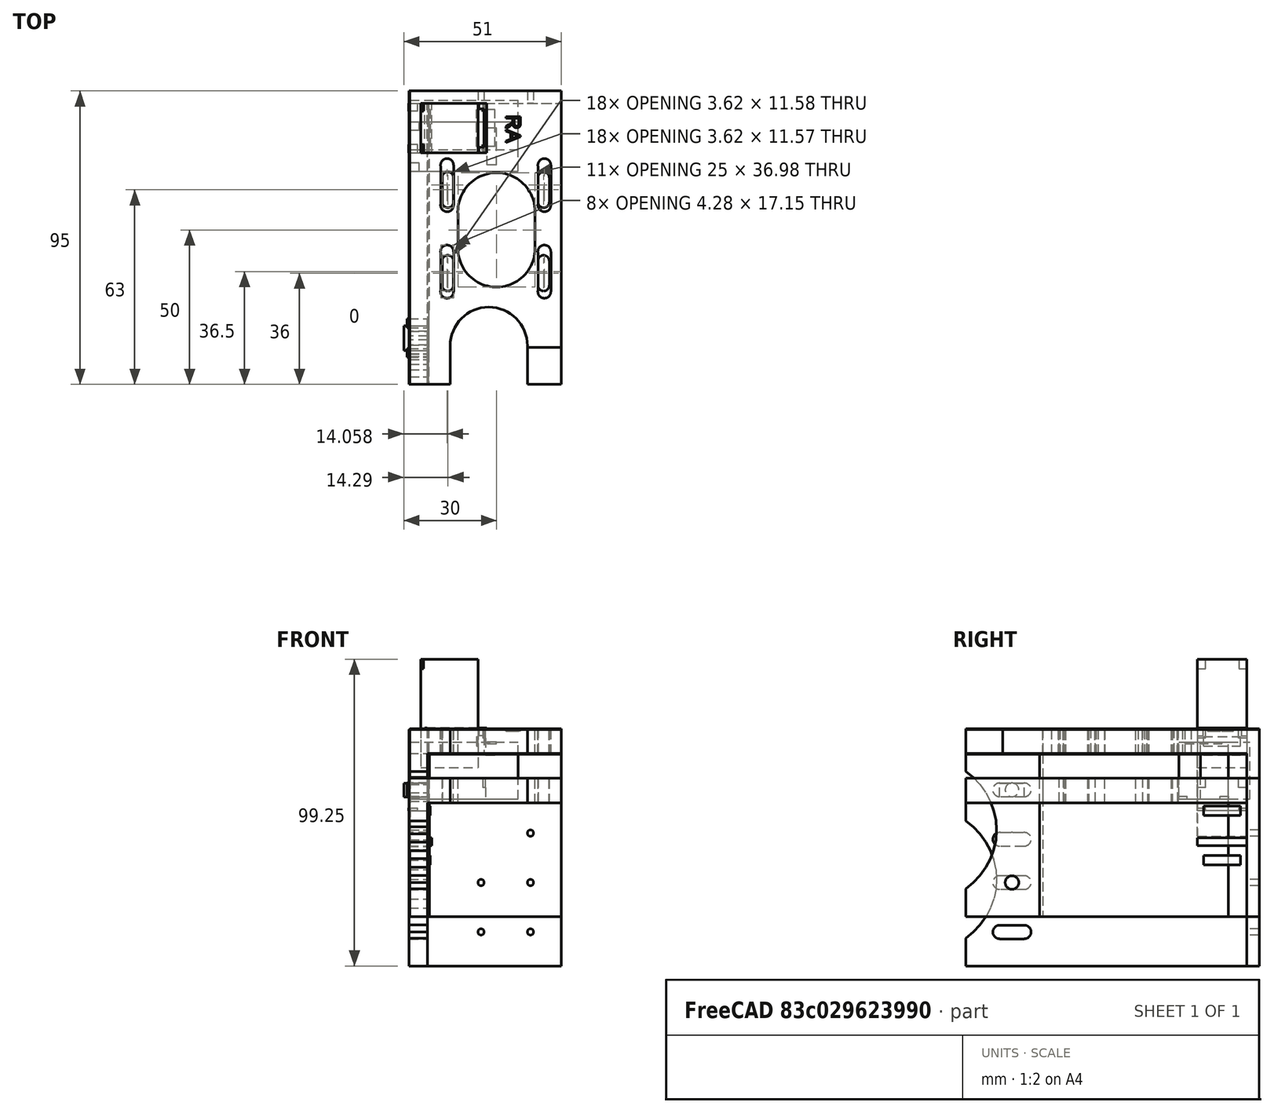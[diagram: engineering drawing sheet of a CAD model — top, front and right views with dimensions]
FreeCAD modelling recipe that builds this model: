
FCSTD DOCUMENT  (FreeCAD 0.17R11223 (Git))
Label: EQ-motorvRAv2
License: All rights reserved
LicenseURL: http://en.wikipedia.org/wiki/All_rights_reserved
objects: Part::Feature×21, Part::Box×16, Part::Cut×14, Part::Cylinder×12, Part::MultiFuse×11, Part::Extrusion×3, Part::Part2DObjectPython×1
note: 78 computed .brp shape members not serialized (recipe doc carries the construction recipe); baked Part::Feature solids carry a one-line shape summary decoded from their .brp

FEATURE [Part::Feature] Cut026_solid  label="zadni stena (Solid)"
  shape: bbox 49 x 4 x 60.5 mm, 8 faces (baked)
FEATURE [Part::Feature] Fusion008_solid  label="Boky"
  shape: bbox 49 x 85 x 60.5 mm, 76 faces (baked)
FEATURE [Part::Box] Box005009  label="Krychle009"
  AttacherType = Attacher::AttachEngine3D
  Height = 18.5
  Length = 35
  Placement = pos=(-5,75,-44) rot=(0,0,1;0rad)
  Width = 16
FEATURE [Part::Box] Box005011  label="Krychle010"
  AttacherType = Attacher::AttachEngine3D
  Height = 2.7
  Length = 3
  Placement = pos=(-5,75,-45.8) rot=(0,0,1;0rad)
  Width = 2.7
FEATURE [Part::Box] Box005012  label="Krychle011"
  AttacherType = Attacher::AttachEngine3D
  Height = 2.7
  Length = 3
  Placement = pos=(-5,88.4,-45.8) rot=(0,0,1;0rad)
  Width = 2.7
FEATURE [Part::Box] Box005014  label="Krychle013"
  AttacherType = Attacher::AttachEngine3D
  Height = 2
  Length = 3
  Placement = pos=(20,77,-26) rot=(0,0,1;0rad)
  Width = 12
FEATURE [Part::Box] Box005015  label="Pro RJ"
  AttacherType = Attacher::AttachEngine3D
  Height = 18.5
  Length = 35
  Placement = pos=(-5,82,-44) rot=(0,0,1;0rad)
  Width = 16
FEATURE [Part::Box] Box005016  label="Krychle014"
  AttacherType = Attacher::AttachEngine3D
  Height = 8
  Length = 49
  Placement = pos=(-5,91,-29.5) rot=(0,0,1;0rad)
  Width = 6
FEATURE [Part::Box] Box005017  label="Krychle015"
  AttacherType = Attacher::AttachEngine3D
  Height = 60
  Length = 6
  Placement = pos=(-5,91,-82) rot=(0,0,1;0rad)
  Width = 6
FEATURE [Part::MultiFuse] Fusion
  Shapes = -> [Box005017,Box005016,Cut026_solid,Fusion008_solid]
FEATURE [Part::Feature] Fusion_solid  label="Fusion (Solid)"
  shape: bbox 49 x 95 x 60.5 mm, 91 faces (baked)
FEATURE [Part::Feature] Fusion_solid001  label="Fusion (Solid)001"
  shape: bbox 49 x 95 x 60.5 mm, 72 faces (baked)
FEATURE [Part::Feature] Fusion_solid_cs  label="REZ A"
  shape: bbox 49 x 95 x 4e-07 mm, 0 faces, 0 solids (baked)
FEATURE [Part::Feature] Fusion_solid001_cs  label="REZ B"
  shape: bbox 5e-07 x 95 x 60.5 mm, 0 faces, 0 solids (baked)
FEATURE [Part::Feature] Cut026_solid001  label="zadni stena (Solid)001"
  shape: bbox 49 x 4 x 60.5 mm, 8 faces (baked)
FEATURE [Part::Extrusion] Extrude  label="Vrsek"
  Base = -> Fusion_solid_cs
  Dir = (0,0,1)
  DirMode = 2
  FaceMakerClass = Part::FaceMakerBullseye
  LengthFwd = 8
  LengthRev = 0
  Placement = pos=(0,0,-2.5) rot=(0,0,1;0rad)
  Solid = true
  Symmetric = false
FEATURE [Part::Extrusion] Extrude001  label="Bok"
  Base = -> Fusion_solid001_cs
  Dir = (1,0,0)
  DirMode = 2
  FaceMakerClass = Part::FaceMakerBullseye
  LengthFwd = 6
  LengthRev = 0
  Placement = pos=(-1.8,0,0) rot=(0,0,1;0rad)
  Solid = true
  Symmetric = false
FEATURE [Part::MultiFuse] Fusion001
  Shapes = -> [Cut026_solid001,Extrude,Extrude001]
FEATURE [Part::Feature] Fusion001001  label="Fusion002"
  shape: bbox 49.3 x 95 x 60.75 mm, 66 faces (baked)
FEATURE [Part::Feature] Fusion001001_solid  label="Drzak Bez RJ"
  shape: bbox 49.3 x 95 x 60.75 mm, 66 faces (baked)
FEATURE [Part::Box] Box005018  label="Krychle016"
  AttacherType = Attacher::AttachEngine3D
  Height = 16
  Length = 31.5
  Placement = pos=(1,81,-22) rot=(0,1,0;1.5708rad)
  Width = 15.5
FEATURE [Part::Cut] Cut
  Base = -> Box005009
  Tool = -> Box005011
FEATURE [Part::Cut] Cut001
  Base = -> Cut
  Tool = -> Box005012
FEATURE [Part::Cut] Cut002  label="Pro RJ001"
  Base = -> Cut001
  Tool = -> Box005014
FEATURE [Part::Feature] Cut002_solid  label="Pro RJ001 (Solid)"
  Placement = pos=(42.5,6,-3.75) rot=(0,1,0;1.5708rad)
  shape: bbox 18.5 x 16 x 35 mm, 17 faces (baked)
FEATURE [Part::Feature] Cut003001_solid  label="EQ motorDe V3"
  shape: bbox 49.5 x 95 x 60.75 mm, 85 faces (baked)
FEATURE [Part::Feature] Cut002_solid001  label="Pro RJ001 (Solid)001"
  Placement = pos=(18,178,-22.5) rot=(0,0,1;3.14159rad)
  shape: bbox 18.5 x 16 x 35 mm, 17 faces (baked)
FEATURE [Part::MultiFuse] Fusion001002
  Shapes = -> [Box005018,Fusion001001_solid]
FEATURE [Part::Cut] Cut003
  Base = -> Fusion001002
  Tool = -> Cut002_solid001
FEATURE [Part::Feature] Cut003001  label="RA V2"
  shape: bbox 49.3 x 95 x 60.75 mm, 81 faces, 2 solids (baked)
FEATURE [Part::Cylinder] Cylinder  label="Válec"
  Angle = 360
  AttacherType = Attacher::AttachEngine3D
  Height = 7
  Placement = pos=(-6,25,-41) rot=(0,1,0;1.5708rad)
  Radius = 2.2
FEATURE [Part::Cylinder] Cylinder001  label="Válec001"
  Angle = 360
  AttacherType = Attacher::AttachEngine3D
  Height = 7
  Placement = pos=(-6,17,-41) rot=(0,1,0;1.5708rad)
  Radius = 2.2
FEATURE [Part::Box] Box  label="Krychle"
  AttacherType = Attacher::AttachEngine3D
  Height = 4.4
  Length = 8
  Placement = pos=(-7,17,-43.3) rot=(0,0,1;0rad)
  Width = 8
FEATURE [Part::MultiFuse] Fusion001003
  Shapes = -> [Cylinder001,Cylinder,Box]
FEATURE [Part::Feature] Fusion001003001  label="DIRA 010"
  shape: bbox 8 x 12.4 x 4.5 mm, 10 faces (baked)
FEATURE [Part::Feature] Fusion001003002  label="DIRA 011"
  Placement = pos=(0,0,-30) rot=(0,0,1;0rad)
  shape: bbox 8 x 12.4 x 4.5 mm, 10 faces (baked)
FEATURE [Part::Cut] Cut003002
  Base = -> Cut003001
  Tool = -> Fusion001003001
FEATURE [Part::Cut] Cut003003
  Base = -> Cut003002
  Placement = pos=(0,0,-16) rot=(0,0,1;0rad)
  Tool = -> Fusion001003002
FEATURE [Part::Feature] Cut003003001  label="RA V4"
  shape: bbox 49.3 x 95 x 60.75 mm, 95 faces, 2 solids (baked)
FEATURE [Part::Box] Box005019  label="Krychle017"
  AttacherType = Attacher::AttachEngine3D
  Height = 10
  Length = 15
  Placement = pos=(31,5,-30) rot=(0,0,1;0rad)
  Width = 13
FEATURE [Part::Cut] Cut003003002
  Base = -> Cut003003001
  Tool = -> Box005019
FEATURE [Part::Feature] Cut003003002001  label="Cut003003003"
  shape: bbox 49.3 x 95 x 60.75 mm, 95 faces, 2 solids (baked)
FEATURE [Part::Cylinder] Cylinder002  label="Válec002"
  Angle = 360
  AttacherType = Attacher::AttachEngine3D
  Height = 4
  Placement = pos=(18,101,-71) rot=(1,0,0;1.5708rad)
  Radius = 1
FEATURE [Part::Cylinder] Cylinder003  label="Válec003"
  Angle = 360
  AttacherType = Attacher::AttachEngine3D
  Height = 4
  Placement = pos=(34,101,-55) rot=(1,0,0;1.5708rad)
  Radius = 1
FEATURE [Part::MultiFuse] Fusion001003003
  Shapes = -> [Cut003003002001,Cylinder002]
FEATURE [Part::Cut] Cut003003002002
  Base = -> Fusion001003003
  Tool = -> Cylinder003
FEATURE [Part::Feature] Cut003003002002001  label="EQ RA V3"
  shape: bbox 49.3 x 95 x 60.75 mm, 95 faces, 2 solids (baked)
FEATURE [Part::Cylinder] Cylinder004  label="Válec004"
  Angle = 360
  AttacherType = Attacher::AttachEngine3D
  Height = 10
  Radius = 2.1
FEATURE [Part::Cylinder] Cylinder005  label="Válec005"
  Angle = 360
  AttacherType = Attacher::AttachEngine3D
  Height = 10
  Placement = pos=(0,13,0) rot=(0,0,1;0rad)
  Radius = 2.1
FEATURE [Part::Box] Box005020  label="Krychle018"
  AttacherType = Attacher::AttachEngine3D
  Height = 10
  Length = 4.2
  Placement = pos=(-2,0,0) rot=(0,0,1;0rad)
  Width = 13
FEATURE [Part::MultiFuse] Fusion001003004  label="Dira M"
  Placement = pos=(7,36,-30) rot=(0,0,1;0rad)
  Shapes = -> [Cylinder004,Cylinder005,Box005020]
FEATURE [Part::Cylinder] Cylinder006  label="Válec006"
  Angle = 360
  AttacherType = Attacher::AttachEngine3D
  Height = 10
  Radius = 2.1
FEATURE [Part::Cylinder] Cylinder007  label="Válec007"
  Angle = 360
  AttacherType = Attacher::AttachEngine3D
  Height = 10
  Placement = pos=(0,13,0) rot=(0,0,1;0rad)
  Radius = 2.1
FEATURE [Part::Box] Box005021  label="Krychle019"
  AttacherType = Attacher::AttachEngine3D
  Height = 10
  Length = 4.2
  Placement = pos=(-2,0,0) rot=(0,0,1;0rad)
  Width = 13
FEATURE [Part::MultiFuse] Fusion001003005  label="Dira M001"
  Placement = pos=(38.5,36,-30) rot=(0,0,1;0rad)
  Shapes = -> [Cylinder006,Cylinder007,Box005021]
FEATURE [Part::Cylinder] Cylinder008  label="Válec008"
  Angle = 360
  AttacherType = Attacher::AttachEngine3D
  Height = 10
  Radius = 2.1
FEATURE [Part::Cylinder] Cylinder009  label="Válec009"
  Angle = 360
  AttacherType = Attacher::AttachEngine3D
  Height = 10
  Placement = pos=(0,13,0) rot=(0,0,1;0rad)
  Radius = 2.1
FEATURE [Part::Box] Box005022  label="Krychle020"
  AttacherType = Attacher::AttachEngine3D
  Height = 10
  Length = 4.2
  Placement = pos=(-2,0,0) rot=(0,0,1;0rad)
  Width = 13
FEATURE [Part::MultiFuse] Fusion001003006  label="Dira M002"
  Placement = pos=(7,64,-30) rot=(0,0,1;0rad)
  Shapes = -> [Cylinder008,Cylinder009,Box005022]
FEATURE [Part::Cylinder] Cylinder010  label="Válec010"
  Angle = 360
  AttacherType = Attacher::AttachEngine3D
  Height = 10
  Radius = 2.1
FEATURE [Part::Cylinder] Cylinder011  label="Válec011"
  Angle = 360
  AttacherType = Attacher::AttachEngine3D
  Height = 10
  Placement = pos=(0,13,0) rot=(0,0,1;0rad)
  Radius = 2.1
FEATURE [Part::Box] Box005023  label="Krychle021"
  AttacherType = Attacher::AttachEngine3D
  Height = 10
  Length = 4.2
  Placement = pos=(-2,0,0) rot=(0,0,1;0rad)
  Width = 13
FEATURE [Part::MultiFuse] Fusion001003007  label="Dira M003"
  Placement = pos=(38.5,64,-30) rot=(0,0,1;0rad)
  Shapes = -> [Cylinder010,Cylinder011,Box005023]
FEATURE [Part::Box] Box009  label="Doraz003"
  AttacherType = Attacher::AttachEngine3D
  Height = 2.5
  Length = 2
  Placement = pos=(0,81,-59) rot=(0,0,1;0rad)
  Width = 16
FEATURE [Part::Feature] Cut003001_solid001  label="EQ motor V3"
  shape: bbox 49.5 x 95 x 60.75 mm, 85 faces (baked)
FEATURE [Part::Feature] Cut005_solid002002005  label="RJ45 M DE002"
  Placement = pos=(6,12,-80) rot=(0,1,0;1.5708rad)
  shape: bbox 18.45 x 15.95 x 35 mm, 12 faces (baked)
FEATURE [Part::Box] Box005024  label="Krychle022"
  AttacherType = Attacher::AttachEngine3D
  Height = 20
  Length = 8.05
  Placement = pos=(-0.2,81,-21) rot=(0,1,0;1.5708rad)
  Width = 16
FEATURE [Part::MultiFuse] Fusion001003008
  Shapes = -> [Cut003003002002001]
FEATURE [Part::Cut] Cut003003002002002
  Base = -> Fusion001003008
  Tool = -> Fusion001003004
FEATURE [Part::Cut] Cut003003002002003
  Base = -> Cut003003002002002
  Tool = -> Fusion001003005
FEATURE [Part::Cut] Cut003003002002004
  Base = -> Cut003003002002003
  Tool = -> Fusion001003006
FEATURE [Part::Cut] Cut003003002002005  label="Oravene diry"
  Base = -> Cut003003002002004
  Tool = -> Fusion001003007
FEATURE [Part::MultiFuse] Fusion001003009
  Shapes = -> [Box009,Box005024,Cut003003002002005]
FEATURE [Part::Cut] Cut003003002002006  label="RA MOTOR"
  Base = -> Fusion001003009
  Tool = -> Cut005_solid002002005
FEATURE [Part::Part2DObjectPython] ShapeString  # Draft 2D object (typed FeaturePython)
  FontFile = Z:/A8 ZS/FREECAD/ARIAL.TTF
  Placement = pos=(29.7506,88.0389,-21.25) rot=(0,0,1;0rad)
  Size = 5
  String = RA
  Tracking = 0
FEATURE [Part::Extrusion] Extrude002
  Base = -> ShapeString
  Dir = (0,0,1)
  DirMode = 2
  FaceMakerClass = Part::FaceMakerBullseye
  LengthFwd = 0.75
  LengthRev = 0
  Placement = pos=(-62,123,-0.75) rot=(0,0,-1;1.5708rad)
  Solid = false
  Symmetric = false
FEATURE [Part::Cut] Cut003003002002007
  Base = -> Cut003003002002006
  Tool = -> Extrude002
FEATURE [Part::Feature] Cut003003002002007001  label="RA MOTOR HOLDER"
  shape: bbox 49.3 x 95 x 61 mm, 156 faces (baked)
